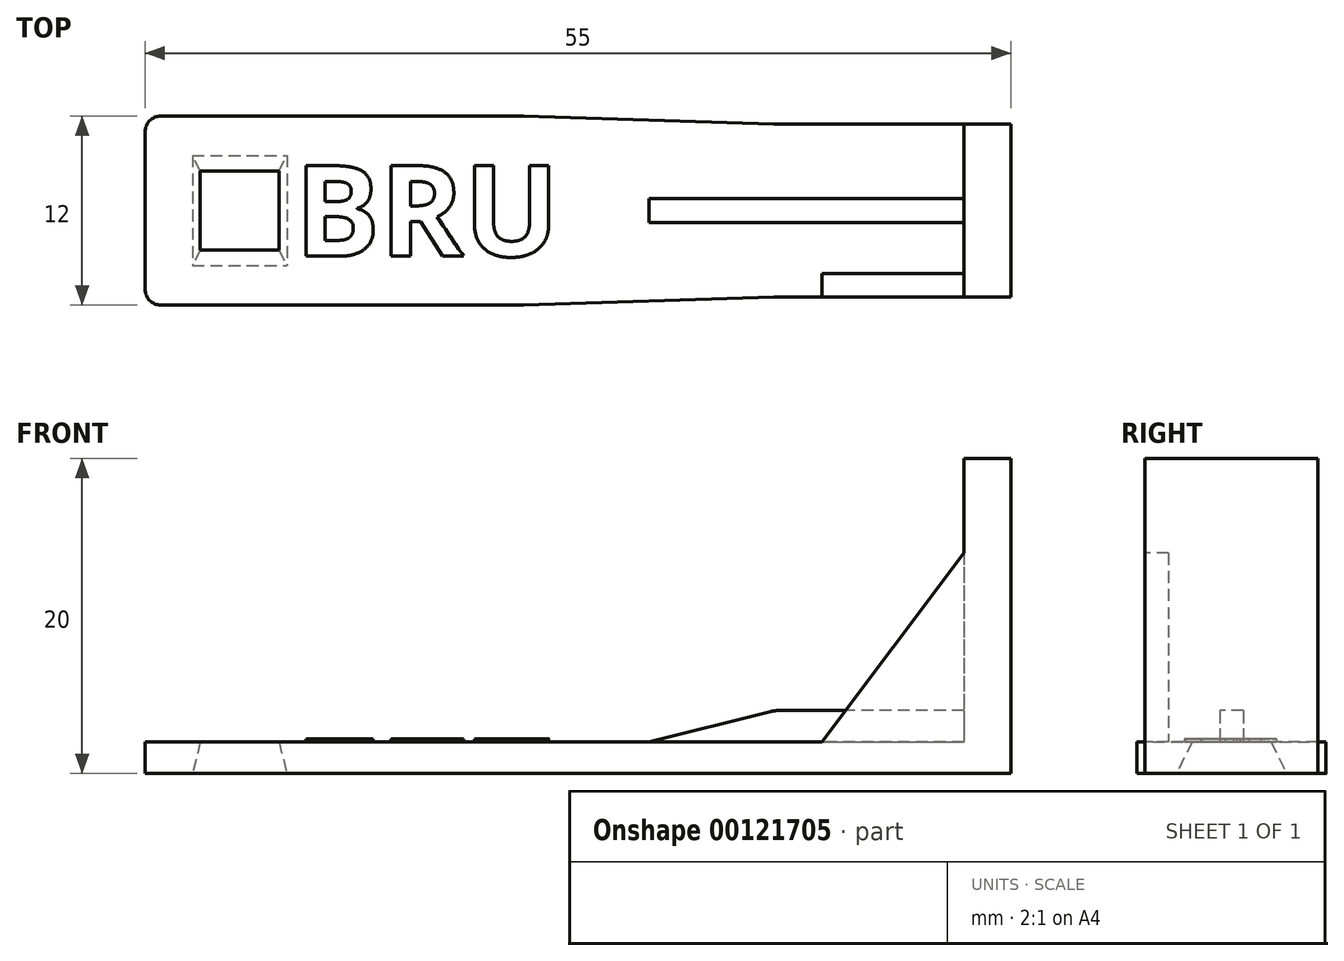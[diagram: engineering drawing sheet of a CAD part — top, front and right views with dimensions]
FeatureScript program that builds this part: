
annotation { "Feature Type Name" : "Feature", "Feature Type Description" : "" }
export const myFeature = defineFeature(function(context is Context, id is Id, definition is map)
    precondition{}
    {
        {
            var Q0;
            Q0=qCreatedBy(makeId("Top.planeOp"),FACE);
            var sketch = newSketch(context, id + "F0", { "sketchPlane" : qUnion([Q0])});
            skLineSegment(sketch, "E0.bottom", {"start": v(-6, -6) * mm, "end": v(6, -6) * mm});
            skLineSegment(sketch, "E0.top", {"start": v(-6, 6) * mm, "end": v(6, 6) * mm});
            skLineSegment(sketch, "E0.left", {"start": v(-6, -6) * mm, "end": v(-6, 6) * mm});
            skLineSegment(sketch, "E0.right", {"start": v(6, -6) * mm, "end": v(6, 6) * mm});
            skPoint(sketch, "E0.middle", {"position": v(0, 0) * mm});
            skLineSegment(sketch, "E1.bottom", {"start": v(6, 6) * mm, "end": v(18, 6) * mm});
            skLineSegment(sketch, "E1.top", {"start": v(6, -6) * mm, "end": v(18, -6) * mm});
            skLineSegment(sketch, "E1.left", {"start": v(6, 6) * mm, "end": v(6, -6) * mm});
            skLineSegment(sketch, "E1.right", {"start": v(18, 6) * mm, "end": v(18, -6) * mm});
            skPoint(sketch, "E2", {"position": v(18, 0) * mm});
            skLineSegment(sketch, "E3.bottom", {"start": v(34, 5.5) * mm, "end": v(49, 5.5) * mm});
            skLineSegment(sketch, "E3.top", {"start": v(34, -5.5) * mm, "end": v(49, -5.5) * mm});
            skLineSegment(sketch, "E3.left", {"start": v(34, 5.5) * mm, "end": v(34, -5.5) * mm});
            skLineSegment(sketch, "E3.right", {"start": v(49, 5.5) * mm, "end": v(49, -5.5) * mm});
            skPoint(sketch, "E4", {"position": v(49, 0) * mm});
            skLineSegment(sketch, "E5", {"start": v(18, 6) * mm, "end": v(34, 5.5) * mm});
            skLineSegment(sketch, "E6", {"start": v(18, -6) * mm, "end": v(34, -5.5) * mm});
            skSolve(sketch);
        }
        {
            var Q0;
            Q0 = qSketchRegion(id + "F0", true);
            extrude(context, id + "F1", {"entities" : qUnion([Q0]), "depth" : 2 * mm});
        }
        {
            var Q0;
            Q0=makeQuery(id+"F1.opExtrude","CAP_FACE",FACE,{"disambiguationData":[OSD([sQuery(id+"F0.wireOp",EDGE,"E0.bottom"),sQuery(id+"F0.wireOp",EDGE,"E0.top"),sQuery(id+"F0.wireOp",EDGE,"E0.left"),sQuery(id+"F0.wireOp",EDGE,"E0.right"),sQuery(id+"F0.wireOp",EDGE,"E1.bottom"),sQuery(id+"F0.wireOp",EDGE,"E1.top"),sQuery(id+"F0.wireOp",EDGE,"E3.bottom"),sQuery(id+"F0.wireOp",EDGE,"E3.top"),sQuery(id+"F0.wireOp",EDGE,"E3.right"),sQuery(id+"F0.wireOp",EDGE,"E5"),sQuery(id+"F0.wireOp",EDGE,"E6")])],"isStart":false});
            var sketch = newSketch(context, id + "F2", { "sketchPlane" : qUnion([Q0])});
            skLineSegment(sketch, "E7.bottom", {"start": v(-2.5, 2.5) * mm, "end": v(2.5, 2.5) * mm});
            skLineSegment(sketch, "E7.top", {"start": v(-2.5, -2.5) * mm, "end": v(2.5, -2.5) * mm});
            skLineSegment(sketch, "E7.left", {"start": v(-2.5, 2.5) * mm, "end": v(-2.5, -2.5) * mm});
            skLineSegment(sketch, "E7.right", {"start": v(2.5, 2.5) * mm, "end": v(2.5, -2.5) * mm});
            skPoint(sketch, "E7.middle", {"position": v(0, 0) * mm});
            skSolve(sketch);
        }
        {
            var Q0;
            Q0=makeQuery(id+"F1.opExtrude","CAP_FACE",FACE,{"disambiguationData":[OSD([sQuery(id+"F0.wireOp",EDGE,"E0.bottom"),sQuery(id+"F0.wireOp",EDGE,"E0.top"),sQuery(id+"F0.wireOp",EDGE,"E0.left"),sQuery(id+"F0.wireOp",EDGE,"E0.right"),sQuery(id+"F0.wireOp",EDGE,"E1.bottom"),sQuery(id+"F0.wireOp",EDGE,"E1.top"),sQuery(id+"F0.wireOp",EDGE,"E3.bottom"),sQuery(id+"F0.wireOp",EDGE,"E3.top"),sQuery(id+"F0.wireOp",EDGE,"E3.right"),sQuery(id+"F0.wireOp",EDGE,"E5"),sQuery(id+"F0.wireOp",EDGE,"E6")])],"isStart":true});
            var sketch = newSketch(context, id + "F3", { "sketchPlane" : qUnion([Q0])});
            skLineSegment(sketch, "E8.bottom", {"start": v(-3, -3.5) * mm, "end": v(3, -3.5) * mm});
            skLineSegment(sketch, "E8.top", {"start": v(-3, 3.5) * mm, "end": v(3, 3.5) * mm});
            skLineSegment(sketch, "E8.left", {"start": v(-3, -3.5) * mm, "end": v(-3, 3.5) * mm});
            skLineSegment(sketch, "E8.right", {"start": v(3, -3.5) * mm, "end": v(3, 3.5) * mm});
            skPoint(sketch, "E8.middle", {"position": v(0, 0) * mm});
            skSolve(sketch);
        }
        {
            var Q1;
            Q1=makeQuery(id+"F2.imprint","IMPRINT",FACE,{"disambiguationData":[TD([[makeQuery(id+"F2.imprint","IMPRINT",EDGE,{"derivedFrom":sQuery(id+"F2.wireOp",EDGE,"E7.bottom")}),-1.0]])]});
            var Q2;
            Q2=makeQuery(id+"F3.imprint","IMPRINT",FACE,{"disambiguationData":[TD([[makeQuery(id+"F3.imprint","IMPRINT",EDGE,{"derivedFrom":sQuery(id+"F3.wireOp",EDGE,"E8.bottom")}),1.0]])]});
            loft(context, id + "F4", {"operationType" : NewBodyOperationType.REMOVE, "sheetProfilesArray" : [{ "sheetProfileEntities" : qUnion([Q1]) }, { "sheetProfileEntities" : qUnion([Q2]) }]});
        }
        {
            var Q0;
            Q0=makeQuery(id+"F1.opExtrude","CAP_FACE",FACE,{"disambiguationData":[OSD([sQuery(id+"F0.wireOp",EDGE,"E0.bottom"),sQuery(id+"F0.wireOp",EDGE,"E0.top"),sQuery(id+"F0.wireOp",EDGE,"E0.left"),sQuery(id+"F0.wireOp",EDGE,"E0.right"),sQuery(id+"F0.wireOp",EDGE,"E1.bottom"),sQuery(id+"F0.wireOp",EDGE,"E1.top"),sQuery(id+"F0.wireOp",EDGE,"E3.bottom"),sQuery(id+"F0.wireOp",EDGE,"E3.top"),sQuery(id+"F0.wireOp",EDGE,"E3.right"),sQuery(id+"F0.wireOp",EDGE,"E5"),sQuery(id+"F0.wireOp",EDGE,"E6")])],"isStart":false});
            var sketch = newSketch(context, id + "F5", { "sketchPlane" : qUnion([Q0])});
            skLineSegment(sketch, "E9.bottom", {"start": v(49, 5.5) * mm, "end": v(46, 5.5) * mm});
            skLineSegment(sketch, "E9.top", {"start": v(49, -5.5) * mm, "end": v(46, -5.5) * mm});
            skLineSegment(sketch, "E9.left", {"start": v(49, 5.5) * mm, "end": v(49, -5.5) * mm});
            skLineSegment(sketch, "E9.right", {"start": v(46, 5.5) * mm, "end": v(46, -5.5) * mm});
            skSolve(sketch);
        }
        {
            var Q0;
            Q0=makeQuery(id+"F5.imprint","IMPRINT",FACE,{"disambiguationData":[TD([[makeQuery(id+"F5.imprint","IMPRINT",EDGE,{"derivedFrom":sQuery(id+"F5.wireOp",EDGE,"E9.bottom")}),-1.0]])]});
            extrude(context, id + "F6", {"entities" : qUnion([Q0]), "operationType" : NewBodyOperationType.ADD, "depth" : 18 * mm});
        }
        {
            var Q0;
            Q0=makeQuery(id+"F6.boolean.opBoolean","MERGE",FACE,{"derivedFrom":[makeQuery(id+"F1.opExtrude","SWEPT_FACE",FACE,{"disambiguationData":[OSD([sQuery(id+"F0.wireOp",EDGE,"E3.top")])]}),makeQuery(id+"F6.opExtrude","SWEPT_FACE",FACE,{"disambiguationData":[OSD([sQuery(id+"F5.wireOp",EDGE,"E9.top")])]})]});
            var sketch = newSketch(context, id + "F7", { "sketchPlane" : qUnion([Q0])});
            skLineSegment(sketch, "E10", {"start": v(37, 2) * mm, "end": v(46, 14) * mm});
            skSolve(sketch);
        }
        {
            var Q0;
            {var subQ0=sQuery(id+"F7.wireOp",EDGE,"E10");Q0=makeQuery(id+"F7.imprint","IMPRINT",FACE,{"disambiguationData":[TD([[makeQuery(id+"F7.imprint","IMPRINT",EDGE,{"derivedFrom":subQ0}),-1.0]])]});}
            extrude(context, id + "F8", {"entities" : qUnion([Q0]), "operationType" : NewBodyOperationType.ADD, "oppositeDirection" : true, "depth" : 1.5 * mm});
        }
        {
            var Q0;
            Q0=makeQuery(id+"F1.opExtrude","CAP_FACE",FACE,{"disambiguationData":[OSD([sQuery(id+"F0.wireOp",EDGE,"E0.bottom"),sQuery(id+"F0.wireOp",EDGE,"E0.top"),sQuery(id+"F0.wireOp",EDGE,"E0.left"),sQuery(id+"F0.wireOp",EDGE,"E0.right"),sQuery(id+"F0.wireOp",EDGE,"E1.bottom"),sQuery(id+"F0.wireOp",EDGE,"E1.top"),sQuery(id+"F0.wireOp",EDGE,"E3.bottom"),sQuery(id+"F0.wireOp",EDGE,"E3.top"),sQuery(id+"F0.wireOp",EDGE,"E3.right"),sQuery(id+"F0.wireOp",EDGE,"E5"),sQuery(id+"F0.wireOp",EDGE,"E6")])],"isStart":false});
            var sketch = newSketch(context, id + "F9", { "sketchPlane" : qUnion([Q0])});
            skLineSegment(sketch, "E11.bottom", {"start": v(46, 0.75) * mm, "end": v(34, 0.75) * mm});
            skLineSegment(sketch, "E11.top", {"start": v(46, -0.75) * mm, "end": v(34, -0.75) * mm});
            skLineSegment(sketch, "E11.left", {"start": v(46, 0.75) * mm, "end": v(46, -0.75) * mm});
            skLineSegment(sketch, "E11.right", {"start": v(34, 0.75) * mm, "end": v(34, -0.75) * mm});
            skPoint(sketch, "E12", {"position": v(46, 0) * mm});
            skSolve(sketch);
        }
        {
            var Q0;
            Q0 = qSketchRegion(id + "F9", true);
            var Q1;
            Q1=makeQuery(id+"F9.imprint","IMPRINT",FACE,{"disambiguationData":[TD([[makeQuery(id+"F9.imprint","IMPRINT",EDGE,{"derivedFrom":sQuery(id+"F9.wireOp",EDGE,"E11.bottom")}),1.0]])]});
            extrude(context, id + "F10", {"entities" : qUnion([Q0, Q1]), "operationType" : NewBodyOperationType.ADD, "depth" : 2 * mm});
        }
        {
            var Q0;
            Q0=makeQuery(id+"F10.opExtrude","SWEPT_FACE",FACE,{"disambiguationData":[OSD([sQuery(id+"F9.wireOp",EDGE,"E11.top")])]});
            var sketch = newSketch(context, id + "F11", { "sketchPlane" : qUnion([Q0])});
            skLineSegment(sketch, "E13.0", {"start": v(18, 2) * mm, "end": v(34, 2) * mm});
            skLineSegment(sketch, "E14.0", {"start": v(18, 2) * mm, "end": v(18, 2) * mm});
            skLineSegment(sketch, "E15", {"start": v(34, 4) * mm, "end": v(26, 2) * mm});
            skSolve(sketch);
        }
        {
            var Q0;
            Q0 = qSketchRegion(id + "F11", true);
            var Q1;
            {var subQ0=sQuery(id+"F11.wireOp",EDGE,"E13.0");Q1=makeQuery(id+"F11.imprint","IMPRINT",FACE,{"disambiguationData":[TD([[makeQuery(id+"F11.imprint","IMPRINT",EDGE,{"derivedFrom":subQ0}),1.0]])]});}
            extrude(context, id + "F12", {"entities" : qUnion([Q0, Q1]), "operationType" : NewBodyOperationType.ADD, "oppositeDirection" : true, "depth" : 1.5 * mm});
        }
        {
            var Q0;
            Q0=makeQuery(id+"F8.opExtrude","SWEPT_EDGE",EDGE,{"disambiguationData":[OSD([sQuery(id+"F0.wireOp",EDGE,"E3.top"),sQuery(id+"F7.wireOp",EDGE,"E10")])]});
            var Q1;
            Q1=makeQuery(id+"FWDOhXmkCX4GDuQ_1.1.F8.opExtrude","SWEPT_EDGE",EDGE,{"disambiguationData":[OSD([sQuery(id+"F0.wireOp",EDGE,"E3.top"),sQuery(id+"F7.wireOp",EDGE,"E10")])]});
            var Q2;
            Q2=makeQuery(id+"FWDOhXmkCX4GDuQ_1.1.F8.opExtrude","SWEPT_EDGE",EDGE,{"disambiguationData":[OSD([sQuery(id+"F0.wireOp",EDGE,"E3.top"),sQuery(id+"F5.wireOp",EDGE,"E9.top"),sQuery(id+"F5.wireOp",EDGE,"E9.right"),sQuery(id+"F7.wireOp",EDGE,"E10")])]});
            var Q3;
            Q3=makeQuery(id+"F8.opExtrude","SWEPT_EDGE",EDGE,{"disambiguationData":[OSD([sQuery(id+"F0.wireOp",EDGE,"E3.top"),sQuery(id+"F5.wireOp",EDGE,"E9.top"),sQuery(id+"F5.wireOp",EDGE,"E9.right"),sQuery(id+"F7.wireOp",EDGE,"E10")])]});
            var Q4;
            {var subQ0=sQuery(id+"F9.wireOp",EDGE,"E11.right");Q4=makeQuery(id+"F12.boolean.opBoolean","MERGE",EDGE,{"derivedFrom":[makeQuery(id+"F10.opExtrude","CAP_EDGE",EDGE,{"disambiguationData":[OSD([subQ0])],"isStart":false}),makeQuery(id+"F12.opExtrude","SWEPT_EDGE",EDGE,{"disambiguationData":[OSD([sQuery(id+"F9.wireOp",EDGE,"E11.top"),subQ0,sQuery(id+"F11.wireOp",EDGE,"E15")])]})]});}
            var Q5;
            Q5=makeQuery(id+"F12.opExtrude","SWEPT_EDGE",EDGE,{"disambiguationData":[OSD([sQuery(id+"F11.wireOp",EDGE,"E13.0"),sQuery(id+"F11.wireOp",EDGE,"E15")])]});
            var Q6;
            Q6=makeQuery(id+"F1.opExtrude","SWEPT_EDGE",EDGE,{"disambiguationData":[OSD([sQuery(id+"F0.wireOp",EDGE,"E1.top"),sQuery(id+"F0.wireOp",EDGE,"E1.right"),sQuery(id+"F0.wireOp",EDGE,"E6")])]});
            var Q7;
            Q7=makeQuery(id+"F1.opExtrude","SWEPT_EDGE",EDGE,{"disambiguationData":[OSD([sQuery(id+"F0.wireOp",EDGE,"E3.top"),sQuery(id+"F0.wireOp",EDGE,"E3.left"),sQuery(id+"F0.wireOp",EDGE,"E6")])]});
            var Q8;
            Q8=makeQuery(id+"F1.opExtrude","SWEPT_EDGE",EDGE,{"disambiguationData":[OSD([sQuery(id+"F0.wireOp",EDGE,"E3.bottom"),sQuery(id+"F0.wireOp",EDGE,"E3.left"),sQuery(id+"F0.wireOp",EDGE,"E5")])]});
            var Q9;
            Q9=makeQuery(id+"F1.opExtrude","SWEPT_EDGE",EDGE,{"disambiguationData":[OSD([sQuery(id+"F0.wireOp",EDGE,"E1.bottom"),sQuery(id+"F0.wireOp",EDGE,"E1.right"),sQuery(id+"F0.wireOp",EDGE,"E5")])]});
            fillet(context, id + "F13", {"entities" : qUnion([Q0, Q1, Q2, Q3, Q4, Q5, Q6, Q7, Q8, Q9]), "radius" : 3 * mm, "tangentPropagation" : true, "allowEdgeOverflow" : false});
        }
        {
            var Q0;
            Q0=makeQuery(id+"F1.opExtrude","SWEPT_EDGE",EDGE,{"disambiguationData":[OSD([sQuery(id+"F0.wireOp",EDGE,"E0.top"),sQuery(id+"F0.wireOp",EDGE,"E0.left")])]});
            var Q1;
            Q1=makeQuery(id+"F1.opExtrude","SWEPT_EDGE",EDGE,{"disambiguationData":[OSD([sQuery(id+"F0.wireOp",EDGE,"E0.bottom"),sQuery(id+"F0.wireOp",EDGE,"E0.left")])]});
            fillet(context, id + "F14", {"entities" : qUnion([Q0, Q1]), "radius" : 1 * mm, "tangentPropagation" : true, "allowEdgeOverflow" : false});
        }
        {
            var Q0;
            Q0=makeQuery(id+"F1.opExtrude","CAP_FACE",FACE,{"disambiguationData":[OSD([sQuery(id+"F0.wireOp",EDGE,"E0.bottom"),sQuery(id+"F0.wireOp",EDGE,"E0.top"),sQuery(id+"F0.wireOp",EDGE,"E0.left"),sQuery(id+"F0.wireOp",EDGE,"E1.bottom"),sQuery(id+"F0.wireOp",EDGE,"E1.top"),sQuery(id+"F0.wireOp",EDGE,"E3.bottom"),sQuery(id+"F0.wireOp",EDGE,"E3.top"),sQuery(id+"F0.wireOp",EDGE,"E3.right"),sQuery(id+"F0.wireOp",EDGE,"E5"),sQuery(id+"F0.wireOp",EDGE,"E6")])],"isStart":false});
            var sketch = newSketch(context, id + "F15", { "sketchPlane" : qUnion([Q0])});
            skText(sketch, "E16", { "text": "BRU", "fontName": "OpenSans-Bold.ttf"});
            skPoint(sketch, "E17", {"position": v(3.5, 0) * mm});
            const initialGuessF15  = {"E16": [0.0035, -0.0029, 1, 0, 0.0058]};
            skSetInitialGuess(sketch, initialGuessF15);
            skSolve(sketch);
        }
        {
            var Q0;
            Q0 = qSketchRegion(id + "F15", true);
            extrude(context, id + "F16", {"entities" : qUnion([Q0]), "operationType" : NewBodyOperationType.ADD, "depth" : 0.2 * mm});
        }
    });
